# Revit family: EZSTL8WSS2K
name_source: partatom
category: Plumbing Fixtures
units: mm (PartAtom-declared; Revit-internal decimal feet)

## family parameters
Always vertical = Yes
Cut with Voids When Loaded = No
Part Type = Normal
Room Calculation Point = No
Round Connector Dimension = Use Diameter
Shared = No
Work Plane-Based = No

## types (1)
- EZSTL8WSS2K
    Activation by = Electronic Bottle Filler Sensor With Electronic Front And Side Bubbler Pushbar
    Approx. Shipping Weight = 89 lbs
    Bubbler Style = Flexi-Guard ® Safety Bubbler
    Chilling Capacity = 8.0 GPH
    Dimensions (L x W x H) = 36 3/4 inch x 19 inch x 39-1/16 inch
    Finish = Stainless Steel
    Full Load Amps = 3
    Installation Location = Indoor
    Manufacturer = Elkay
    Model = EZSTL8WSS2K
    Mounting Type = Wall Mount (On Wall)
    Number of Stations = 2
    Power = 220V/50Hz
    Rated Watts = 370
    Special Features = Hands Free, Green Ticker™, Laminar Flow, Antimicrobial, Real Drain
    Version = 1.0.0.0

## geometry (parser evidence)
native form markers: Sweep x20
no freeform markers — native parametric forms only
